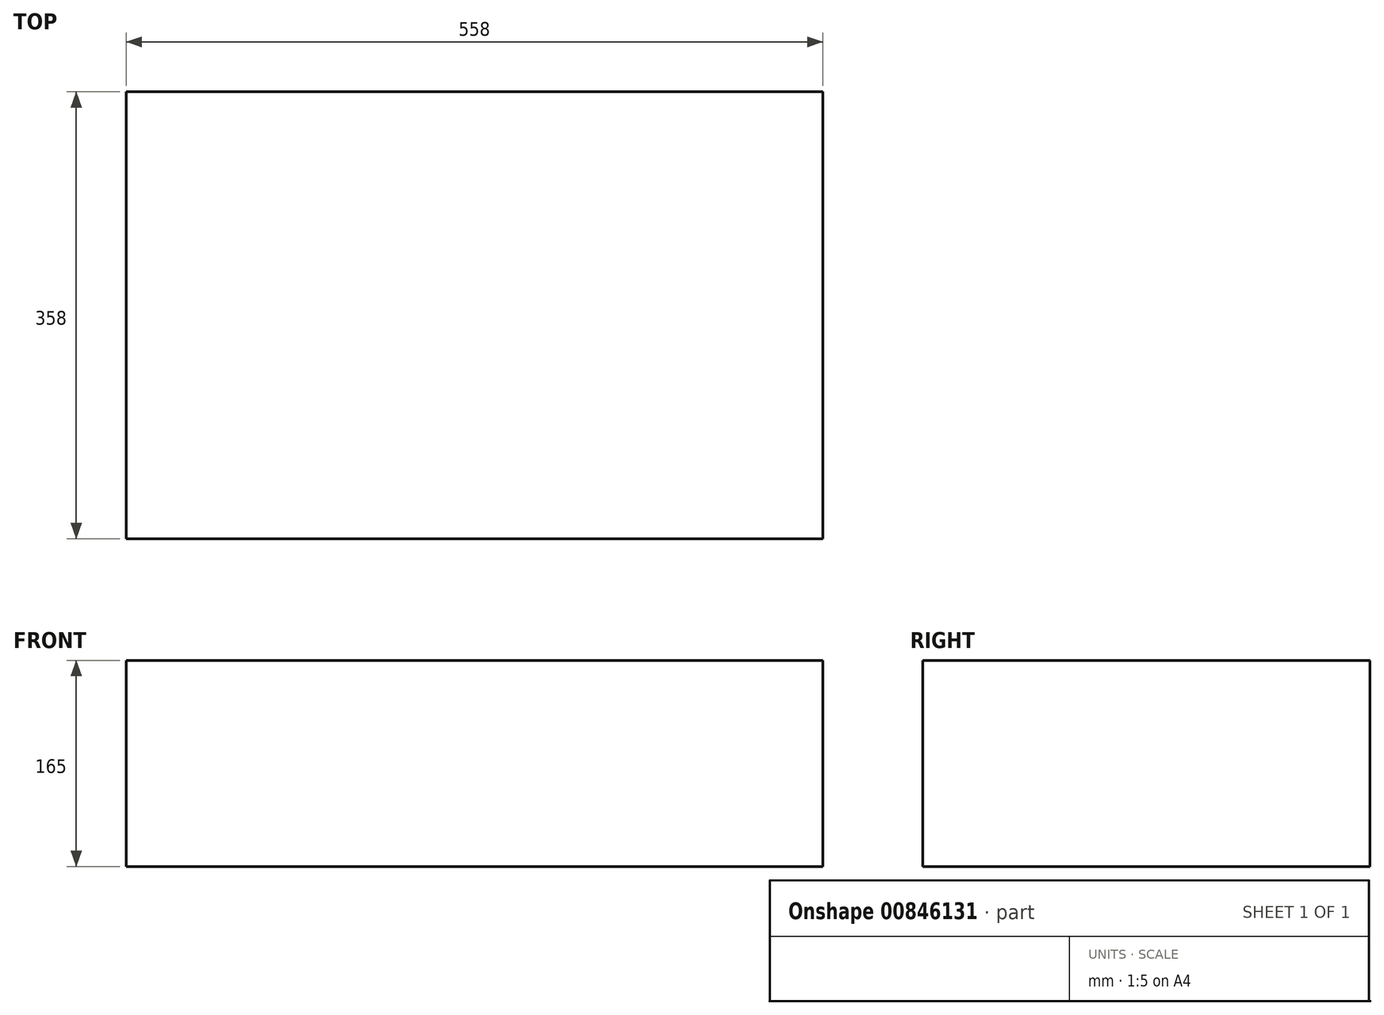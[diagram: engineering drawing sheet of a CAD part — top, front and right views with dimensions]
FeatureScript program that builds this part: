
annotation { "Feature Type Name" : "Feature", "Feature Type Description" : "" }
export const myFeature = defineFeature(function(context is Context, id is Id, definition is map)
    precondition{}
    {
        {
            var Q0;
            Q0=qCreatedBy(makeId("Top.planeOp"),FACE);
            var sketch = newSketch(context, id + "F0", { "sketchPlane" : qUnion([Q0])});
            skLineSegment(sketch, "E0.bottom", {"start": v(-276.04, 209.94) * mm, "end": v(281.96, 209.94) * mm});
            skLineSegment(sketch, "E0.top", {"start": v(-276.04, -148.06) * mm, "end": v(281.96, -148.06) * mm});
            skLineSegment(sketch, "E0.left", {"start": v(-276.04, 209.94) * mm, "end": v(-276.04, -148.06) * mm});
            skLineSegment(sketch, "E0.right", {"start": v(281.96, 209.94) * mm, "end": v(281.96, -148.06) * mm});
            skSolve(sketch);
        }
        {
            var Q0;
            Q0=makeQuery(id+"F0.imprint","IMPRINT",FACE,{"disambiguationData":[TD([[makeQuery(id+"F0.imprint","IMPRINT",EDGE,{"derivedFrom":sQuery(id+"F0.wireOp",EDGE,"E0.bottom")}),-1.0]])]});
            extrude(context, id + "F1", {"entities" : qUnion([Q0]), "depth" : 165 * mm, "offsetDistance" : 25 * mm});
        }
    });
